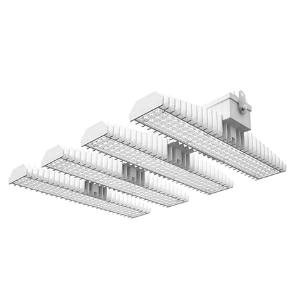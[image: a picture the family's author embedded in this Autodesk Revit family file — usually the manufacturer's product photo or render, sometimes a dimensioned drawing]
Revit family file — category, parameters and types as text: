
# Revit family: 3f_filippi_-_3f_lem_ho_ampio_3f_filippi_-_58956_a0811_-_3f_lem_4_ho_led_280_cr_ampio___vt_a363
name_source: partatom
category: Lighting Fixtures
units: mm (PartAtom-declared; Revit-internal decimal feet)

## family parameters
Cut with Voids When Loaded = No
Host = Face
Light Source = No
Part Type = Normal
Room Calculation Point = No
Round Connector Dimension = Use Diameter
Shared = No

## types (1)
- 3F Filippi - 3F LEM HO Ampio (1 x LED, 42103 lm, 276 W, 4000 K)
    Apparent Load = 276 VA
    Approval mark = CE
    CIE Flux Codes = 60 92 99 100 100
    Color Rendering = 80
    Color Temperature = 4000 K
    Control Gear = Electronic ballast
    Default Elevation = 1800 mm
    Description = Industrial luminaire with high light output and high luminous efficiency designed with the most innovative technologies for environments with temperature up to 55°C.

ILLUMINOTECHNICAL
Luminous efficiency 100% (DLOR 99%, ULOR 1%).
Initial luminous flux of the luminaire 42103 lm.
Direct symmetric wide distribution: the illuminated area has a rectangular shape.
Installation Interdistance Transv.D = 1.58 x hu - Long.D = 1.45 x hu.
Tabular UGR (CIE 117 - 4H-8H; S=0.25H; 70/50/20): RUG 23.9 - 24.9.
Beam angle: 93° - 99°.
Luminous efficacy 153 lm/W.
Lifetime (L93/B10): 30000 h. (tq+25°C)
Lifetime (L90/B10): 50000 h. (tq+25°C)
Lifetime (L85/B10): 80000 h. (tq+25°C)
Lifetime (L80/B10): 100000 h. (tq+25°C)
Lifetime (L85/B10): 50000 h. (tq+55°C)
Sudden decreased luminous flux after 50000 hours: 0% (C0).
Photobiological safety in compliance with IEC/TR 62778: RG0 risk exempt, (IEC 62471).
In compliance with IEC/EN 62722-2-1 - IEC/EN 62717 standards.

SOURCE
4 Mid-Power linear LED modules 70W/840.
Energy efficiency class (UE 2019/2020 - UE 2019/2015): C.
CIE 13.3 Colour rendering index: CRI >80 (R9 <50%).
IES TM-30 Fidelity Index: Rf = 84 Rg = 95.
CCT nominal colour temperature 4000 K.
Colour initial tolerance (MacAdam): SDCM 3.

MECHANICAL
Passive modular heatsinks in die-casted aluminium, painted in white colour.
To optimize the thermal management of the LED module, the heatsinks are oversized and provided with self-cleaning of cooling fins.
Wiring body in aluminium and galvanised steel anchored solidly to the sinks and thermally separated.
3F Lens lenses with high luminous efficiency, transparent methacrylate (PMMA), fixed to the LED modules.
Fixing brackets in stainless steel.
Luminaire with limited surface temperature. - D - (EN 60598-2-24)
Dimensions: 757x542 mm, height 133 mm. Weight 19.373 kg.
IP65 protection degree.
Mechanical strength to impacts IK06 (1 joule).
Glow-wire test resistance 650°C.

ELECTRICAL
Halogen Free electronic wiring 230V-50/60Hz, power factor 0.97, THD <25%, constant output current, class I, 2 driver.
Power of the luminaire 276 W.
ENEC - CE.
SAFE FLICKER: PstLM=<1 and SVM=<0.4 (IEC TR 61547-1 and IEC TR 63158), to ensure a more comfortable and safe light.
Luminaire compliant with EN 60598-2-22 for power supply from a centralised emergency system CPSS (Central Power Supply System), not incorporated in the luminaire - high risk areas excluded. The default power and flux are 100% in AC and 100% in DC.
Ambient temperature from -30°C to +55°C.
Temperature class T6 max 85°C.
Quick connection via M20 3P connector with 9-13 mm tightening range.
Power unit positioned on a separate compartment by the LED module to ensure optimum temperatures of cabling components, to be inspectable and maintainable.
Relative humidity UR: <85%.

INSTALLATION
Ceiling / Suspended / Wall.
All accessories dedicated to this product are available on the Catalog and on our website www.3F-Filippi.com.

ACCESSORIES
A0811 - VT transparent glass, tempered, not flammable, with sealing gasket.
One required for each light module. The pack contains 10 pieces.

APPLICATIONS
In commercial environments, exhibition and industrial areas, stores, open areas.
Environments in which it is necessary a total protection against falling fragments (eg environments with foodstuffs or machines with moving parts or with extreme temperature changes), use luminaires with polycarbonate lenses.

WARNING
Fixture not suitable for cold stores with an ambient temperature <0°C and/or relative humidity >85%.
Luminaire designed for disposal/recycling at end-of-life.
Replaceable (LED only) light source by a professional. Replaceable control gear by a professional.
    Height = 133 mm  [stored 0.436352 ft]
    Lamp = 1 x LED
    Lamp Light Flux = 42103 lm
    Lamp Power = 276 W
    Lamp count = 1
    Length = 757 mm
    Lifetime = 50000 h
    Luminous efficacy = 153 lm/W
    Manufacturer = 3F Filippi
    ModVariant = No
    Model = 3F Filippi - 58956+A0811 - 3F LEM 4 HO LED 280 CR AMPIO + VT
    Mounting Place = Ceiling
    Mounting Type = Pendant
    Number of Poles = 1
    OnlyDefault = Yes
    Power Factor = 1
    Product Name = 3F Filippi - 3F LEM HO Ampio
    Product group = pendant luminaire
    ProductGroupID = 9
    Protection Class = Protection class I
    Protection Degree = IP 65
    RLX_Detail_Level = 1
    RLX_Emergency_Light_Flux = 0 lm
    RLX_Emergency_Type = 0
    RLX_Emergency_Type_DB = No
    RlxData = <blob elided: 118209 chars, md5=d906801d>
    Socket = socket
    Standby Power = 0 W
    System Light Flux = 42103 lm
    System Power = 276 W
    Type Comments = Product without accessories
    Type Image = 3f_filippi_-_lem_4__a0811.jpg
    URL = http://relux.com
    VarID = ---
    Voltage = 0 V
    Weight = 0.00 kg
    Width = 542 mm

note: [stored X ft] marks values corroborated as IEEE doubles in the binary element streams (Revit-internal decimal feet)

## geometry (parser evidence)
native form markers: Blend x4, Sweep x12
no freeform markers — native parametric forms only
